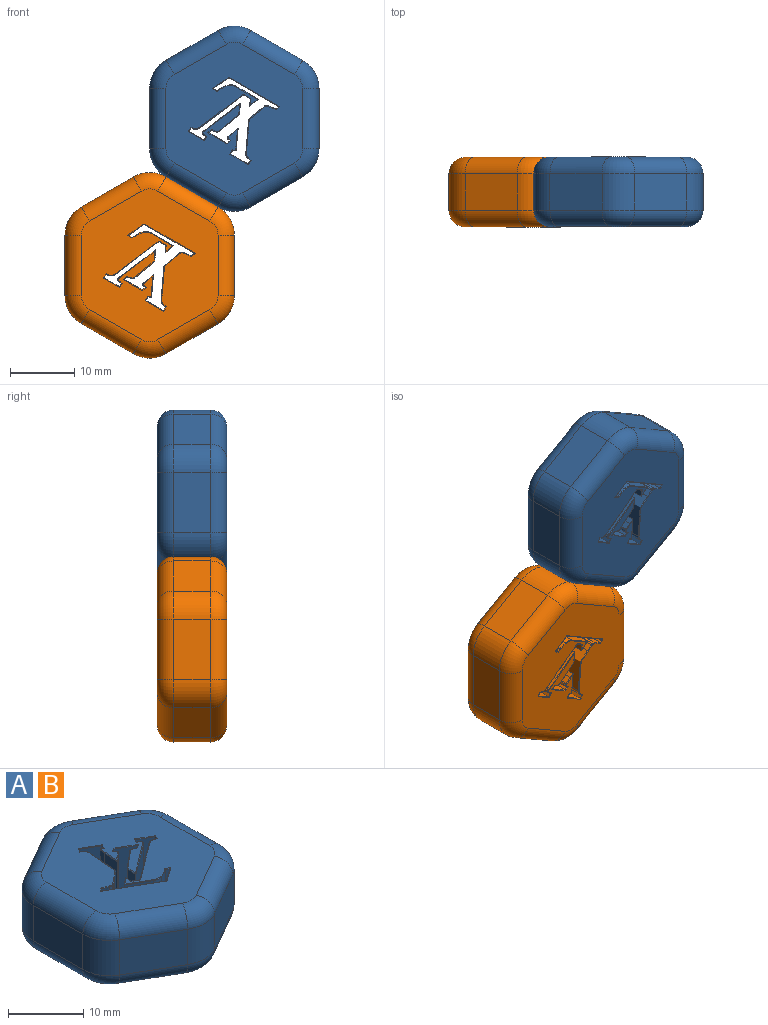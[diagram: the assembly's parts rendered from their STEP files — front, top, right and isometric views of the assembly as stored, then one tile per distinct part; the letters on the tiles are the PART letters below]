
ASSEMBLY  parts=2 mates=1
PART A: 224 faces, bbox 27.2x29.7x10.8 mm
  f0: plane 23.83x21.32mm, normal (0,0,1), area 341.9mm2, adj f14,f15,f16,f17,f18,f19,f20,f21
  f1: plane 23.83x21.32mm, normal (0,0,-1), area 341.9mm2, adj f26,f27,f28,f29,f30,f31,f32,f33
  f2: plane 8.12x5.76mm, normal (-0.5,-0.87,0), area 54mm2, adj f8,f13,f25,f37
  f3: plane 8.12x5.76mm, normal (0.5,-0.87,0), area 54mm2, adj f8,f9,f22,f34
  f4: plane 9.37x5.76mm, normal (1,0,0), area 54mm2, adj f9,f10,f18,f30
  f5: plane 8.12x5.76mm, normal (0.5,0.87,0), area 54mm2, adj f10,f11,f14,f26
  f6: plane 8.12x5.76mm, normal (-0.5,0.87,0), area 54mm2, adj f11,f12,f17,f29
  f7: plane 9.37x5.76mm, normal (-1,0,0), area 54mm2, adj f12,f13,f21,f33
  f8: cylinder r=5.08mm len=5.76mm, axis (0,0,-1), area 30.6mm2, adj f2,f3,f24,f36
  f9: cylinder r=5.08mm len=5.76mm, axis (0,0,-1), area 30.6mm2, adj f3,f4,f20,f32
  f10: cylinder r=5.08mm len=5.76mm, axis (0,0,-1), area 30.6mm2, adj f4,f5,f16,f28
  f11: cylinder r=5.08mm len=5.76mm, axis (0,0,-1), area 30.6mm2, adj f5,f6,f15,f27
  f12: cylinder r=5.08mm len=5.76mm, axis (0,0,-1), area 30.6mm2, adj f6,f7,f19,f31
  f13: cylinder r=5.08mm len=5.76mm, axis (0,0,-1), area 30.6mm2, adj f2,f7,f23,f35
  f14: cylinder r=2.54mm len=9.39mm, axis (0.87,-0.5,0), area 37.4mm2, adj f0,f5,f15,f16
  f15: torus R=2.54mm, axis (0,0,1), area 17.4mm2, adj f0,f11,f14,f17
  f16: torus R=2.54mm, axis (0,0,1), area 17.4mm2, adj f0,f10,f14,f18
  f17: cylinder r=2.54mm len=9.39mm, axis (0.87,0.5,0), area 37.4mm2, adj f0,f6,f15,f19
  f18: cylinder r=2.54mm len=9.37mm, axis (0,-1,0), area 37.4mm2, adj f0,f4,f16,f20
  f19: torus R=2.54mm, axis (0,0,1), area 17.4mm2, adj f0,f12,f17,f21
  f20: torus R=2.54mm, axis (0,0,1), area 17.4mm2, adj f0,f9,f18,f22
  f21: cylinder r=2.54mm len=9.37mm, axis (0,1,0), area 37.4mm2, adj f0,f7,f19,f23
  f22: cylinder r=2.54mm len=9.39mm, axis (-0.87,-0.5,0), area 37.4mm2, adj f0,f3,f20,f24
  f23: torus R=2.54mm, axis (0,0,1), area 17.4mm2, adj f0,f13,f21,f25
  f24: torus R=2.54mm, axis (0,0,1), area 17.4mm2, adj f0,f8,f22,f25
  f25: cylinder r=2.54mm len=9.39mm, axis (-0.87,0.5,0), area 37.4mm2, adj f0,f2,f23,f24
  f26: cylinder r=2.54mm len=9.39mm, axis (-0.87,0.5,0), area 37.4mm2, adj f1,f5,f27,f28
  f27: torus R=2.54mm, axis (0,0,1), area 17.4mm2, adj f1,f11,f26,f29
  f28: torus R=2.54mm, axis (0,0,1), area 17.4mm2, adj f1,f10,f26,f30
  f29: cylinder r=2.54mm len=9.39mm, axis (-0.87,-0.5,0), area 37.4mm2, adj f1,f6,f27,f31
  f30: cylinder r=2.54mm len=9.37mm, axis (0,1,0), area 37.4mm2, adj f1,f4,f28,f32
  f31: torus R=2.54mm, axis (0,0,1), area 17.4mm2, adj f1,f12,f29,f33
  f32: torus R=2.54mm, axis (0,0,1), area 17.4mm2, adj f1,f9,f30,f34
  f33: cylinder r=2.54mm len=9.37mm, axis (0,-1,0), area 37.4mm2, adj f1,f7,f31,f35
  f34: cylinder r=2.54mm len=9.39mm, axis (0.87,0.5,0), area 37.4mm2, adj f1,f3,f32,f36
  f35: torus R=2.54mm, axis (0,0,1), area 17.4mm2, adj f1,f13,f33,f37
  f36: torus R=2.54mm, axis (0,0,1), area 17.4mm2, adj f1,f8,f34,f37
  f37: cylinder r=2.54mm len=9.39mm, axis (0.87,-0.5,0), area 37.4mm2, adj f1,f2,f35,f36
  f38: extruded ~10.66x0.07mm, area 1mm2, adj f39,f97,f155,f213
  f39: extruded ~10.66x0.87mm, area 12.1mm2, adj f38,f40,f157,f211
  f40: extruded ~10.66x0.63mm, area 8.8mm2, adj f39,f41,f159,f209
  f41: plane 10.66x2.61mm, normal (-1,0.09,0), area 27.9mm2, adj f40,f42,f160,f207
  f42: extruded ~10.66x0.7mm, area 7.4mm2, adj f41,f43,f158,f204
  f43: extruded ~10.66x0.33mm, area 5.6mm2, adj f42,f44,f156,f202
  f44: extruded ~10.66x0.23mm, area 2.7mm2, adj f43,f45,f154,f200
  f45: plane 10.66x0.59mm, normal (-0.87,0.5,0), area 7.3mm2, adj f44,f46,f152,f198
  f46: plane 10.66x2.74mm, normal (-0.5,-0.87,0), area 33.7mm2, adj f45,f47,f150,f196
  f47: plane 10.66x0.59mm, normal (0.87,-0.5,0), area 7.2mm2, adj f46,f48,f148,f194
  f48: extruded ~10.66x0.34mm, area 4.5mm2, adj f47,f49,f146,f192
  f49: extruded ~10.66x0.82mm, area 10mm2, adj f48,f50,f144,f190
  f50: extruded ~10.66x6.64mm, area 79mm2, adj f49,f51,f138,f140,f142,f184,f186,f188
  f51: extruded ~10.66x0.83mm, area 11.6mm2, adj f50,f52,f136,f182
  f52: extruded ~10.66x0.25mm, area 2.9mm2, adj f51,f53,f134,f180
  f53: extruded ~10.66x0.47mm, area 5.1mm2, adj f52,f54,f132,f178
  f54: extruded ~10.66x1.15mm, area 13.5mm2, adj f53,f55,f130,f176
  f55: extruded ~10.66x0.33mm, area 4.6mm2, adj f54,f56,f128,f174
  f56: extruded ~10.66x0.09mm, area 1.3mm2, adj f55,f57,f125,f172
  f57: extruded ~10.66x7.75mm, area 95.4mm2, adj f56,f58,f123,f170
  f58: extruded ~10.66x0.1mm, area 1.2mm2, adj f57,f59,f121,f168
  f59: extruded ~10.66x2.32mm, area 30.1mm2, adj f58,f60,f119,f166
  f60: extruded ~10.66x0.06mm, area 0.8mm2, adj f59,f61,f117,f164
  f61: extruded ~10.66x0.54mm, area 6.6mm2, adj f60,f62,f115,f162
  f62: extruded ~10.66x0.07mm, area 0.8mm2, adj f61,f63,f113,f161
  f63: extruded ~10.66x0.38mm, area 4.9mm2, adj f62,f64,f111,f163
  f64: extruded ~10.66x1.15mm, area 13.6mm2, adj f63,f65,f109,f165
  f65: extruded ~10.66x1.38mm, area 15.2mm2, adj f64,f66,f107,f167
  f66: extruded ~10.66x3.49mm, area 42.9mm2, adj f65,f67,f105,f169
  f67: plane 10.66x1.33mm, normal (-0.64,0.77,0), area 18.3mm2, adj f66,f68,f103,f171
  f68: plane 10.66x1.1mm, normal (1,-0.06,0), area 11.7mm2, adj f67,f69,f101,f173
  f69: extruded ~10.66x0.09mm, area 1.2mm2, adj f68,f70,f99,f175
  f70: extruded ~10.66x0.92mm, area 11.4mm2, adj f69,f71,f98,f177
  f71: extruded ~10.66x0.06mm, area 0.6mm2, adj f70,f72,f100,f179
  f72: extruded ~10.66x0.32mm, area 4.2mm2, adj f71,f73,f102,f181
  f73: extruded ~10.66x7.65mm, area 99.7mm2, adj f72,f74,f104,f183
  f74: extruded ~10.66x0.23mm, area 2.7mm2, adj f73,f75,f106,f185
  f75: extruded ~10.66x0.47mm, area 5.7mm2, adj f74,f76,f108,f187
  f76: extruded ~10.66x0.11mm, area 1.4mm2, adj f75,f77,f110,f189
  f77: extruded ~10.66x2.23mm, area 27.5mm2, adj f76,f78,f112,f191
  f78: extruded ~10.66x0.06mm, area 0.8mm2, adj f77,f79,f114,f193
  f79: plane 10.66x0.53mm, normal (0.87,-0.5,0), area 6.5mm2, adj f78,f80,f116,f195
  f80: extruded ~10.66x0.13mm, area 1.7mm2, adj f79,f81,f118,f197
  f81: extruded ~10.66x0.8mm, area 11.3mm2, adj f80,f82,f120,f199
  f82: extruded ~10.66x0.08mm, area 1mm2, adj f81,f83,f122,f201
  f83: extruded ~10.66x0.18mm, area 2.3mm2, adj f82,f84,f124,f203
  f84: extruded ~10.66x5.44mm, area 72.6mm2, adj f83,f85,f126,f206
  f85: extruded ~10.66x0.07mm, area 1mm2, adj f84,f86,f127,f205
  f86: plane 10.66x1.76mm, normal (-1,0.09,0), area 18.9mm2, adj f85,f87,f129,f208
  f87: extruded ~10.66x0.06mm, area 0.8mm2, adj f86,f88,f131,f133,f210,f212
  f88: extruded ~10.66x3.04mm, area 42.2mm2, adj f87,f89,f135,f214
  f89: extruded ~10.66x0.49mm, area 5.5mm2, adj f88,f90,f137,f216
  f90: extruded ~10.66x0.66mm, area 7.6mm2, adj f89,f91,f139,f218
  f91: extruded ~10.66x0.1mm, area 1.1mm2, adj f90,f92,f141,f220
  f92: extruded ~10.66x0.37mm, area 5.1mm2, adj f91,f93,f143,f222
  f93: extruded ~10.66x0.07mm, area 1mm2, adj f92,f94,f145,f223
  f94: extruded ~10.66x2.87mm, area 34.6mm2, adj f93,f95,f147,f221
  f95: extruded ~10.66x0.43mm, area 6mm2, adj f94,f96,f149,f219
  f96: extruded ~10.66x0.23mm, area 3mm2, adj f95,f97,f151,f217
  f97: extruded ~10.66x0.48mm, area 6mm2, adj f38,f96,f153,f215
  f98: bspline ~1.16x0.72mm, area 0.1mm2, adj f0,f70,f99,f100
  f99: bspline ~0.2x0.17mm, area 0mm2, adj f0,f69,f98,f101
  f100: bspline ~0.12x0.11mm, area 0mm2, adj f0,f71,f98,f102
  f101: cylinder r=0.09mm len=1.1mm, axis (0.06,1,0), area 0.1mm2, adj f0,f68,f99,f103
  f102: bspline ~0.51x0.41mm, area 0.1mm2, adj f0,f72,f100,f104
  f103: cylinder r=0.09mm len=1.38mm, axis (-0.77,-0.64,0), area 0.2mm2, adj f0,f67,f101,f105
  f104: bspline ~12.58x8.44mm, area 1.3mm2, adj f0,f73,f102,f106
  f105: bspline ~4.8x2.83mm, area 0.6mm2, adj f0,f66,f103,f107
  f106: bspline ~0.48x0.29mm, area 0mm2, adj f0,f74,f104,f108
  f107: bspline ~2.05x0.55mm, area 0.2mm2, adj f0,f65,f105,f109
  f108: bspline ~0.94x0.6mm, area 0.1mm2, adj f0,f75,f106,f110
  f109: bspline ~1.57x0.81mm, area 0.2mm2, adj f0,f64,f107,f111
  f110: bspline ~0.25x0.17mm, area 0mm2, adj f0,f76,f108,f112
  f111: bspline ~0.51x0.38mm, area 0.1mm2, adj f0,f63,f109,f113
  f112: bspline ~3.02x1.79mm, area 0.4mm2, adj f0,f77,f110,f114
  f113: bspline ~0.19x0.11mm, area 0mm2, adj f0,f62,f111,f115
  f114: bspline ~0.24x0.18mm, area 0mm2, adj f0,f78,f112,f116
  f115: bspline ~1.09x0.68mm, area 0.1mm2, adj f0,f61,f113,f117
  f116: cylinder r=0.09mm len=0.72mm, axis (0.5,0.87,0), area 0.1mm2, adj f0,f79,f114,f118
  f117: bspline ~0.33x0.29mm, area 0mm2, adj f0,f60,f115,f119
  f118: bspline ~0.3x0.24mm, area 0mm2, adj f0,f80,f116,f120
  f119: bspline ~3.14x2.22mm, area 0.4mm2, adj f0,f59,f117,f121
  f120: bspline ~0.94x0.55mm, area 0.1mm2, adj f0,f81,f118,f122
  f121: bspline ~0.22x0.12mm, area 0mm2, adj f0,f58,f119,f123
  f122: bspline ~0.14x0.13mm, area 0mm2, adj f0,f82,f120,f124
  f123: bspline ~10.55x6.14mm, area 1.3mm2, adj f0,f57,f121,f125
  f124: bspline ~0.27x0.22mm, area 0mm2, adj f0,f83,f122,f126
  f125: bspline ~0.33x0.29mm, area 0mm2, adj f0,f56,f123,f128
  f126: bspline ~7.3x5.54mm, area 0.9mm2, adj f0,f84,f124,f127,f129
  f127: bspline ~0.15x0.14mm, area 0mm2, adj f85,f126,f129
  f128: bspline ~0.46x0.4mm, area 0.1mm2, adj f0,f55,f125,f130
  f129: cylinder r=0.09mm len=1.77mm, axis (-0.09,-1,0), area 0.2mm2, adj f0,f86,f126,f127,f131
  f130: bspline ~1.45x0.61mm, area 0.2mm2, adj f0,f54,f128,f132
  f131: bspline ~0.09x0.09mm, area 0mm2, adj f87,f129,f133
  f132: bspline ~0.57x0.18mm, area 0.1mm2, adj f0,f53,f130,f134
  f133: bspline ~0.09x0.09mm, area 0mm2, adj f0,f87,f131,f135
  f134: bspline ~0.32x0.18mm, area 0mm2, adj f0,f52,f132,f136
  f135: bspline ~4.11x3.45mm, area 0.6mm2, adj f0,f88,f133,f137
  f136: bspline ~1.06x0.92mm, area 0.2mm2, adj f0,f51,f134,f138
  f137: bspline ~0.67x0.23mm, area 0.1mm2, adj f0,f89,f135,f139
  f138: bspline ~2.4x2mm, area 0.3mm2, adj f0,f50,f136,f140
  f139: bspline ~0.82x0.39mm, area 0.1mm2, adj f0,f90,f137,f141
  f140: bspline ~0.09x0.07mm, area 0mm2, adj f50,f138,f142
  f141: bspline ~0.22x0.13mm, area 0mm2, adj f0,f91,f139,f143
  f142: bspline ~8.03x0.8mm, area 0.7mm2, adj f0,f50,f140,f144
  f143: bspline ~0.51x0.44mm, area 0.1mm2, adj f0,f92,f141,f145
  f144: bspline ~1.11x0.49mm, area 0.1mm2, adj f0,f49,f142,f146
  f145: bspline ~0.28x0.26mm, area 0mm2, adj f0,f93,f143,f147
  f146: bspline ~0.72x0.56mm, area 0.1mm2, adj f0,f48,f144,f148
  f147: bspline ~3.83x2.16mm, area 0.5mm2, adj f0,f94,f145,f149
  f148: cylinder r=0.09mm len=0.78mm, axis (0.5,0.87,0), area 0.1mm2, adj f0,f47,f146,f150
  f149: bspline ~0.96x0.83mm, area 0.1mm2, adj f0,f95,f147,f151
  f150: cylinder r=0.09mm len=2.93mm, axis (0.87,-0.5,0), area 0.5mm2, adj f0,f46,f148,f152
  f151: bspline ~0.51x0.41mm, area 0mm2, adj f0,f96,f149,f153
  f152: cylinder r=0.09mm len=0.78mm, axis (-0.5,-0.87,0), area 0.1mm2, adj f0,f45,f150,f154
  f153: bspline ~0.58x0.24mm, area 0.1mm2, adj f0,f97,f151,f155
  f154: bspline ~0.49x0.27mm, area 0mm2, adj f0,f44,f152,f156
  f155: bspline ~0.15x0.14mm, area 0mm2, adj f0,f38,f153,f157
  f156: bspline ~0.45x0.31mm, area 0.1mm2, adj f0,f43,f154,f158
  f157: bspline ~1.1x0.95mm, area 0.2mm2, adj f0,f39,f155,f159
  f158: bspline ~0.85x0.14mm, area 0.1mm2, adj f0,f42,f156,f160
  f159: bspline ~0.86x0.74mm, area 0.1mm2, adj f0,f40,f157,f160
  f160: cylinder r=0.09mm len=2.62mm, axis (-0.09,-1,0), area 0.4mm2, adj f0,f41,f158,f159
  f161: bspline ~0.18x0.1mm, area 0mm2, adj f1,f62,f162,f163
  f162: bspline ~1.09x0.68mm, area 0.1mm2, adj f1,f61,f161,f164
  f163: bspline ~0.51x0.38mm, area 0.1mm2, adj f1,f63,f161,f165
  f164: bspline ~0.33x0.29mm, area 0mm2, adj f1,f60,f162,f166
  f165: bspline ~1.57x0.81mm, area 0.2mm2, adj f1,f64,f163,f167
  f166: bspline ~3.14x2.22mm, area 0.4mm2, adj f1,f59,f164,f168
  f167: bspline ~2.05x0.55mm, area 0.2mm2, adj f1,f65,f165,f169
  f168: bspline ~0.22x0.12mm, area 0mm2, adj f1,f58,f166,f170
  f169: bspline ~3.86x2.29mm, area 0.6mm2, adj f1,f66,f167,f171
  f170: bspline ~10.55x6.14mm, area 1.3mm2, adj f1,f57,f168,f172
  f171: cylinder r=0.09mm len=1.38mm, axis (0.77,0.64,0), area 0.2mm2, adj f1,f67,f169,f173
  f172: bspline ~0.33x0.29mm, area 0mm2, adj f1,f56,f170,f174
  f173: cylinder r=0.09mm len=1.1mm, axis (-0.06,-1,0), area 0.1mm2, adj f1,f68,f171,f175
  f174: bspline ~0.46x0.4mm, area 0.1mm2, adj f1,f55,f172,f176
  f175: bspline ~0.2x0.14mm, area 0mm2, adj f1,f69,f173,f177
  f176: bspline ~1.81x0.73mm, area 0.2mm2, adj f1,f54,f174,f178
  f177: bspline ~1.16x0.72mm, area 0.1mm2, adj f1,f70,f175,f179
  f178: bspline ~0.57x0.16mm, area 0.1mm2, adj f1,f53,f176,f180
  f179: bspline ~0.13x0.12mm, area 0mm2, adj f1,f71,f177,f181
  f180: bspline ~0.31x0.21mm, area 0mm2, adj f1,f52,f178,f182
  f181: bspline ~0.46x0.34mm, area 0.1mm2, adj f1,f72,f179,f183
  f182: bspline ~1.07x0.91mm, area 0.2mm2, adj f1,f51,f180,f184
  f183: bspline ~12.12x8.44mm, area 1.3mm2, adj f1,f73,f181,f185
  f184: bspline ~2.4x2mm, area 0.3mm2, adj f1,f50,f182,f186
  f185: bspline ~0.48x0.29mm, area 0mm2, adj f1,f74,f183,f187
  f186: bspline ~0.09x0.07mm, area 0mm2, adj f50,f184,f188
  f187: bspline ~0.94x0.6mm, area 0.1mm2, adj f1,f75,f185,f189
  f188: bspline ~8.03x0.8mm, area 0.7mm2, adj f1,f50,f186,f190
  f189: bspline ~0.26x0.14mm, area 0mm2, adj f1,f76,f187,f191
  f190: bspline ~1.04x0.63mm, area 0.1mm2, adj f1,f49,f188,f192
  f191: bspline ~2.74x1.63mm, area 0.4mm2, adj f1,f77,f189,f193
  f192: bspline ~0.72x0.56mm, area 0.1mm2, adj f1,f48,f190,f194
  f193: bspline ~0.24x0.18mm, area 0mm2, adj f1,f78,f191,f195
  f194: cylinder r=0.09mm len=0.78mm, axis (-0.5,-0.87,0), area 0.1mm2, adj f1,f47,f192,f196
  f195: cylinder r=0.09mm len=0.72mm, axis (-0.5,-0.87,0), area 0.1mm2, adj f1,f79,f193,f197
  f196: cylinder r=0.09mm len=2.93mm, axis (-0.87,0.5,0), area 0.5mm2, adj f1,f46,f194,f198
  f197: bspline ~0.3x0.24mm, area 0mm2, adj f1,f80,f195,f199
  f198: cylinder r=0.09mm len=0.78mm, axis (0.5,0.87,0), area 0.1mm2, adj f1,f45,f196,f200
  f199: bspline ~0.92x0.66mm, area 0.1mm2, adj f1,f81,f197,f201
  f200: bspline ~0.49x0.27mm, area 0mm2, adj f1,f44,f198,f202
  f201: bspline ~0.14x0.13mm, area 0mm2, adj f1,f82,f199,f203
  f202: bspline ~0.4x0.36mm, area 0.1mm2, adj f1,f43,f200,f204
  f203: bspline ~0.28x0.22mm, area 0mm2, adj f1,f83,f201,f206
  f204: bspline ~0.85x0.14mm, area 0.1mm2, adj f1,f42,f202,f207
  f205: bspline ~0.15x0.14mm, area 0mm2, adj f85,f206,f208
  f206: bspline ~7.3x5.54mm, area 0.9mm2, adj f1,f84,f203,f205,f208
  f207: cylinder r=0.09mm len=2.62mm, axis (0.09,1,0), area 0.4mm2, adj f1,f41,f204,f209
  f208: cylinder r=0.09mm len=1.77mm, axis (0.09,1,0), area 0.2mm2, adj f1,f86,f205,f206,f210
  f209: bspline ~0.96x0.83mm, area 0.1mm2, adj f1,f40,f207,f211
  f210: bspline ~0.09x0.09mm, area 0mm2, adj f87,f208,f212
  f211: bspline ~1.1x0.95mm, area 0.2mm2, adj f1,f39,f209,f213
  f212: bspline ~0.1x0.09mm, area 0mm2, adj f1,f87,f210,f214
  f213: bspline ~0.14x0.14mm, area 0mm2, adj f1,f38,f211,f215
  f214: bspline ~3.73x3.14mm, area 0.6mm2, adj f1,f88,f212,f216
  f215: bspline ~0.58x0.32mm, area 0.1mm2, adj f1,f97,f213,f217
  f216: bspline ~0.65x0.31mm, area 0.1mm2, adj f1,f89,f214,f218
  f217: bspline ~0.51x0.41mm, area 0mm2, adj f1,f96,f215,f219
  f218: bspline ~0.83x0.36mm, area 0.1mm2, adj f1,f90,f216,f220
  f219: bspline ~0.96x0.83mm, area 0.1mm2, adj f1,f95,f217,f221
  f220: bspline ~0.22x0.11mm, area 0mm2, adj f1,f91,f218,f222
  f221: bspline ~3.83x2.16mm, area 0.5mm2, adj f1,f94,f219,f223
  f222: bspline ~0.5x0.44mm, area 0.1mm2, adj f1,f92,f220,f223
  f223: bspline ~0.28x0.26mm, area 0mm2, adj f1,f93,f221,f222
PART B: same geometry as A
PLACE A rot(axis=(0,-0.71,0.71),180deg) t=(-13.05,0,-23)mm
PLACE B rot(axis=(0,-0.71,0.71),180deg) t=(-26.25,0,-45.86)mm
MATE fastened A.f5 <-> B.f2  axis (-0.5,0,-0.87) through (-19.65,-5.42,-34.43)mm
